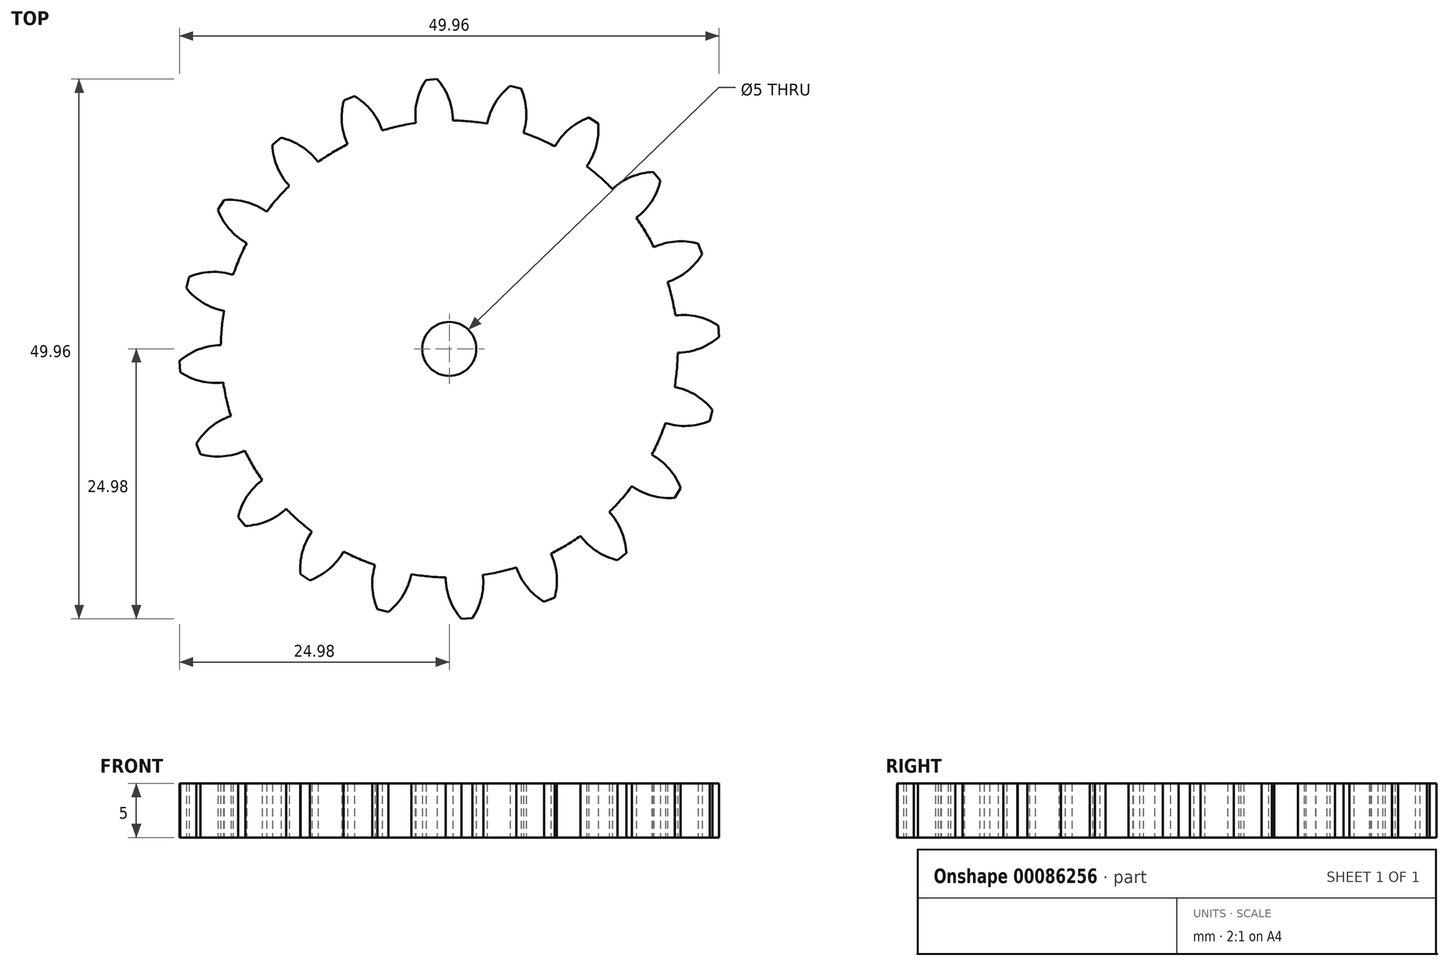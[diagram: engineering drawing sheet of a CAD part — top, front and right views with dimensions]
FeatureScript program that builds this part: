
annotation { "Feature Type Name" : "Feature", "Feature Type Description" : "" }
export const myFeature = defineFeature(function(context is Context, id is Id, definition is map)
    precondition{}
    {
        {
            assignVariable(context, id + "F0", {"name" : "GearDepth", "anyValue" : 5});
        }
        {
            var Q0;
            Q0=qCreatedBy(makeId("Top.planeOp"),FACE);
            var sketch = newSketch(context, id + "F1", { "sketchPlane" : qUnion([Q0])});
            skCircle(sketch, "E0", {"center": v(0, 0) * mm, "radius": 21.15 * mm});
            skCircle(sketch, "E1", {"center": v(0, 0) * mm, "radius": 23.08 * mm, "construction": true});
            skCircle(sketch, "E2", {"center": v(0, 0) * mm, "radius": 25 * mm, "construction": true});
            skLineSegment(sketch, "E3", {"start": v(0, 0) * mm, "end": v(0, 17.6) * mm, "construction": true});
            skLineSegment(sketch, "E4", {"start": v(0, 0) * mm, "end": v(-1.18, 18.01) * mm, "construction": true});
            skLineSegment(sketch, "E5", {"start": v(0, 23.08) * mm, "end": v(-10.54, 23.08) * mm, "construction": true});
            skLineSegment(sketch, "E6", {"start": v(0, 23.08) * mm, "end": v(-10.3, 19.33) * mm, "construction": true});
            skCircle(sketch, "E7", {"center": v(0, 23.08) * mm, "radius": 5.77 * mm, "construction": true});
            skCircle(sketch, "E8", {"center": v(-5.42, 21.1) * mm, "radius": 5.77 * mm, "construction": true});
            skArc(sketch, "E9", {"start": v(-10.84, 23.08) * mm, "mid": v(-10.95, 22.76) * mm, "end": v(-11.04, 22.43) * mm});
            skArc(sketch, "E10.trimOffspring", {"start": v(0.34, 21.15) * mm, "mid": v(-0.04, 23.2) * mm, "end": v(-1.11, 24.98) * mm});
            skArc(sketch, "E11.MirrorCS", {"start": v(-3.1, 20.93) * mm, "mid": v(-2.98, 23) * mm, "end": v(-2.16, 24.9) * mm});
            skLineSegment(sketch, "E12", {"start": v(-2.16, 24.9) * mm, "end": v(-1.11, 24.98) * mm});
            skArc(sketch, "E13.1.0", {"start": v(-6.2, 20.22) * mm, "mid": v(-7.2, 22.05) * mm, "end": v(-8.78, 23.4) * mm});
            skLineSegment(sketch, "E13.1.1", {"start": v(-9.75, 23.02) * mm, "end": v(-8.78, 23.4) * mm});
            skArc(sketch, "E13.1.2", {"start": v(-9.42, 18.94) * mm, "mid": v(-9.95, 20.95) * mm, "end": v(-9.75, 23.02) * mm});
            skArc(sketch, "E13.2.0", {"start": v(-12.15, 17.31) * mm, "mid": v(-13.67, 18.74) * mm, "end": v(-15.58, 19.55) * mm});
            skLineSegment(sketch, "E13.2.1", {"start": v(-16.38, 18.88) * mm, "end": v(-15.58, 19.55) * mm});
            skArc(sketch, "E13.2.2", {"start": v(-14.8, 15.1) * mm, "mid": v(-15.93, 16.85) * mm, "end": v(-16.38, 18.88) * mm});
            skArc(sketch, "E13.3.0", {"start": v(-16.9, 12.71) * mm, "mid": v(-18.79, 13.6) * mm, "end": v(-20.86, 13.78) * mm});
            skLineSegment(sketch, "E13.3.1", {"start": v(-21.42, 12.9) * mm, "end": v(-20.86, 13.78) * mm});
            skArc(sketch, "E13.3.2", {"start": v(-18.75, 9.79) * mm, "mid": v(-20.36, 11.1) * mm, "end": v(-21.42, 12.9) * mm});
            skArc(sketch, "E13.4.0", {"start": v(-20, 6.86) * mm, "mid": v(-22.07, 7.13) * mm, "end": v(-24.1, 6.66) * mm});
            skLineSegment(sketch, "E13.4.1", {"start": v(-24.35, 5.65) * mm, "end": v(-24.1, 6.66) * mm});
            skArc(sketch, "E13.4.2", {"start": v(-20.86, 3.52) * mm, "mid": v(-22.8, 4.27) * mm, "end": v(-24.35, 5.65) * mm});
            skArc(sketch, "E13.5.0", {"start": v(-21.15, 0.34) * mm, "mid": v(-23.2, -0.04) * mm, "end": v(-24.98, -1.11) * mm});
            skLineSegment(sketch, "E13.5.1", {"start": v(-24.9, -2.16) * mm, "end": v(-24.98, -1.11) * mm});
            skArc(sketch, "E13.5.2", {"start": v(-20.93, -3.1) * mm, "mid": v(-23, -2.98) * mm, "end": v(-24.9, -2.16) * mm});
            skArc(sketch, "E13.6.0", {"start": v(-20.22, -6.2) * mm, "mid": v(-22.05, -7.2) * mm, "end": v(-23.4, -8.78) * mm});
            skLineSegment(sketch, "E13.6.1", {"start": v(-23.02, -9.75) * mm, "end": v(-23.4, -8.78) * mm});
            skArc(sketch, "E13.6.2", {"start": v(-18.94, -9.42) * mm, "mid": v(-20.95, -9.95) * mm, "end": v(-23.02, -9.75) * mm});
            skArc(sketch, "E13.7.0", {"start": v(-17.31, -12.15) * mm, "mid": v(-18.74, -13.67) * mm, "end": v(-19.55, -15.58) * mm});
            skLineSegment(sketch, "E13.7.1", {"start": v(-18.88, -16.38) * mm, "end": v(-19.55, -15.58) * mm});
            skArc(sketch, "E13.7.2", {"start": v(-15.1, -14.8) * mm, "mid": v(-16.85, -15.93) * mm, "end": v(-18.88, -16.38) * mm});
            skArc(sketch, "E13.8.0", {"start": v(-12.71, -16.9) * mm, "mid": v(-13.6, -18.79) * mm, "end": v(-13.78, -20.86) * mm});
            skLineSegment(sketch, "E13.8.1", {"start": v(-12.9, -21.42) * mm, "end": v(-13.78, -20.86) * mm});
            skArc(sketch, "E13.8.2", {"start": v(-9.79, -18.75) * mm, "mid": v(-11.1, -20.36) * mm, "end": v(-12.9, -21.42) * mm});
            skArc(sketch, "E13.9.0", {"start": v(-6.86, -20) * mm, "mid": v(-7.13, -22.07) * mm, "end": v(-6.66, -24.1) * mm});
            skLineSegment(sketch, "E13.9.1", {"start": v(-5.65, -24.35) * mm, "end": v(-6.66, -24.1) * mm});
            skArc(sketch, "E13.9.2", {"start": v(-3.52, -20.86) * mm, "mid": v(-4.27, -22.8) * mm, "end": v(-5.65, -24.35) * mm});
            skArc(sketch, "E13.10.0", {"start": v(-0.34, -21.15) * mm, "mid": v(0.04, -23.2) * mm, "end": v(1.11, -24.98) * mm});
            skLineSegment(sketch, "E13.10.1", {"start": v(2.16, -24.9) * mm, "end": v(1.11, -24.98) * mm});
            skArc(sketch, "E13.10.2", {"start": v(3.1, -20.93) * mm, "mid": v(2.98, -23) * mm, "end": v(2.16, -24.9) * mm});
            skArc(sketch, "E13.11.0", {"start": v(6.2, -20.22) * mm, "mid": v(7.2, -22.05) * mm, "end": v(8.78, -23.4) * mm});
            skLineSegment(sketch, "E13.11.1", {"start": v(9.75, -23.02) * mm, "end": v(8.78, -23.4) * mm});
            skArc(sketch, "E13.11.2", {"start": v(9.42, -18.94) * mm, "mid": v(9.95, -20.95) * mm, "end": v(9.75, -23.02) * mm});
            skArc(sketch, "E13.12.0", {"start": v(12.15, -17.31) * mm, "mid": v(13.67, -18.74) * mm, "end": v(15.58, -19.55) * mm});
            skLineSegment(sketch, "E13.12.1", {"start": v(16.38, -18.88) * mm, "end": v(15.58, -19.55) * mm});
            skArc(sketch, "E13.12.2", {"start": v(14.8, -15.1) * mm, "mid": v(15.93, -16.85) * mm, "end": v(16.38, -18.88) * mm});
            skArc(sketch, "E13.13.0", {"start": v(16.9, -12.71) * mm, "mid": v(18.79, -13.6) * mm, "end": v(20.86, -13.78) * mm});
            skLineSegment(sketch, "E13.13.1", {"start": v(21.42, -12.9) * mm, "end": v(20.86, -13.78) * mm});
            skArc(sketch, "E13.13.2", {"start": v(18.75, -9.79) * mm, "mid": v(20.36, -11.1) * mm, "end": v(21.42, -12.9) * mm});
            skArc(sketch, "E13.14.0", {"start": v(20, -6.86) * mm, "mid": v(22.07, -7.13) * mm, "end": v(24.1, -6.66) * mm});
            skLineSegment(sketch, "E13.14.1", {"start": v(24.35, -5.65) * mm, "end": v(24.1, -6.66) * mm});
            skArc(sketch, "E13.14.2", {"start": v(20.86, -3.52) * mm, "mid": v(22.8, -4.27) * mm, "end": v(24.35, -5.65) * mm});
            skArc(sketch, "E13.15.0", {"start": v(21.15, -0.34) * mm, "mid": v(23.2, 0.04) * mm, "end": v(24.98, 1.11) * mm});
            skLineSegment(sketch, "E13.15.1", {"start": v(24.9, 2.16) * mm, "end": v(24.98, 1.11) * mm});
            skArc(sketch, "E13.15.2", {"start": v(20.93, 3.1) * mm, "mid": v(23, 2.98) * mm, "end": v(24.9, 2.16) * mm});
            skArc(sketch, "E13.16.0", {"start": v(20.22, 6.2) * mm, "mid": v(22.05, 7.2) * mm, "end": v(23.4, 8.78) * mm});
            skLineSegment(sketch, "E13.16.1", {"start": v(23.02, 9.75) * mm, "end": v(23.4, 8.78) * mm});
            skArc(sketch, "E13.16.2", {"start": v(18.94, 9.42) * mm, "mid": v(20.95, 9.95) * mm, "end": v(23.02, 9.75) * mm});
            skArc(sketch, "E13.17.0", {"start": v(17.31, 12.15) * mm, "mid": v(18.74, 13.67) * mm, "end": v(19.55, 15.58) * mm});
            skLineSegment(sketch, "E13.17.1", {"start": v(18.88, 16.38) * mm, "end": v(19.55, 15.58) * mm});
            skArc(sketch, "E13.17.2", {"start": v(15.1, 14.8) * mm, "mid": v(16.85, 15.93) * mm, "end": v(18.88, 16.38) * mm});
            skArc(sketch, "E13.18.0", {"start": v(12.71, 16.9) * mm, "mid": v(13.6, 18.79) * mm, "end": v(13.78, 20.86) * mm});
            skLineSegment(sketch, "E13.18.1", {"start": v(12.9, 21.42) * mm, "end": v(13.78, 20.86) * mm});
            skArc(sketch, "E13.18.2", {"start": v(9.79, 18.75) * mm, "mid": v(11.1, 20.36) * mm, "end": v(12.9, 21.42) * mm});
            skArc(sketch, "E13.19.0", {"start": v(6.86, 20) * mm, "mid": v(7.13, 22.07) * mm, "end": v(6.66, 24.1) * mm});
            skLineSegment(sketch, "E13.19.1", {"start": v(5.65, 24.35) * mm, "end": v(6.66, 24.1) * mm});
            skArc(sketch, "E13.19.2", {"start": v(3.52, 20.86) * mm, "mid": v(4.27, 22.8) * mm, "end": v(5.65, 24.35) * mm});
            skCircle(sketch, "E14", {"center": v(0, 0) * mm, "radius": 2.5 * mm});
            skSolve(sketch);
        }
        {
            var Q0;
            {var subQ0=sQuery(id+"F1.wireOp",EDGE,"E10.trimOffspring");Q0=makeQuery(id+"F1.imprint","IMPRINT",FACE,{"disambiguationData":[TD([[makeQuery(id+"F1.imprint","IMPRINT",EDGE,{"derivedFrom":subQ0}),1.0]])]});}
            var Q1;
            {var subQ0=sQuery(id+"F1.wireOp",EDGE,"E0");var subQ1=makeQuery(id+"F1.imprint","INTERSECT",VERTEX,{"derivedFrom":[subQ0,sQuery(id+"F1.wireOp",EDGE,"E10.trimOffspring")]});Q1=makeQuery(id+"F1.imprint","IMPRINT",FACE,{"disambiguationData":[TD([[makeQuery(id+"F1.imprint","IMPRINT",EDGE,{"disambiguationData":[TD([[subQ1,-1.0]])],"derivedFrom":subQ0}),1.0]])]});}
            var Q2;
            {var subQ0=sQuery(id+"F1.wireOp",EDGE,"E13.1.0");Q2=makeQuery(id+"F1.imprint","IMPRINT",FACE,{"disambiguationData":[TD([[makeQuery(id+"F1.imprint","IMPRINT",EDGE,{"derivedFrom":subQ0}),1.0]])]});}
            var Q3;
            {var subQ0=sQuery(id+"F1.wireOp",EDGE,"E13.2.0");Q3=makeQuery(id+"F1.imprint","IMPRINT",FACE,{"disambiguationData":[TD([[makeQuery(id+"F1.imprint","IMPRINT",EDGE,{"derivedFrom":subQ0}),1.0]])]});}
            var Q4;
            {var subQ0=sQuery(id+"F1.wireOp",EDGE,"E13.3.0");Q4=makeQuery(id+"F1.imprint","IMPRINT",FACE,{"disambiguationData":[TD([[makeQuery(id+"F1.imprint","IMPRINT",EDGE,{"derivedFrom":subQ0}),1.0]])]});}
            var Q5;
            {var subQ0=sQuery(id+"F1.wireOp",EDGE,"E13.4.0");Q5=makeQuery(id+"F1.imprint","IMPRINT",FACE,{"disambiguationData":[TD([[makeQuery(id+"F1.imprint","IMPRINT",EDGE,{"derivedFrom":subQ0}),1.0]])]});}
            var Q6;
            {var subQ0=sQuery(id+"F1.wireOp",EDGE,"E13.5.0");Q6=makeQuery(id+"F1.imprint","IMPRINT",FACE,{"disambiguationData":[TD([[makeQuery(id+"F1.imprint","IMPRINT",EDGE,{"derivedFrom":subQ0}),1.0]])]});}
            var Q7;
            {var subQ0=sQuery(id+"F1.wireOp",EDGE,"E13.6.0");Q7=makeQuery(id+"F1.imprint","IMPRINT",FACE,{"disambiguationData":[TD([[makeQuery(id+"F1.imprint","IMPRINT",EDGE,{"derivedFrom":subQ0}),1.0]])]});}
            var Q8;
            {var subQ0=sQuery(id+"F1.wireOp",EDGE,"E13.7.0");Q8=makeQuery(id+"F1.imprint","IMPRINT",FACE,{"disambiguationData":[TD([[makeQuery(id+"F1.imprint","IMPRINT",EDGE,{"derivedFrom":subQ0}),1.0]])]});}
            var Q9;
            {var subQ0=sQuery(id+"F1.wireOp",EDGE,"E13.8.0");Q9=makeQuery(id+"F1.imprint","IMPRINT",FACE,{"disambiguationData":[TD([[makeQuery(id+"F1.imprint","IMPRINT",EDGE,{"derivedFrom":subQ0}),1.0]])]});}
            var Q10;
            {var subQ0=sQuery(id+"F1.wireOp",EDGE,"E13.9.0");Q10=makeQuery(id+"F1.imprint","IMPRINT",FACE,{"disambiguationData":[TD([[makeQuery(id+"F1.imprint","IMPRINT",EDGE,{"derivedFrom":subQ0}),1.0]])]});}
            var Q11;
            {var subQ0=sQuery(id+"F1.wireOp",EDGE,"E13.10.0");Q11=makeQuery(id+"F1.imprint","IMPRINT",FACE,{"disambiguationData":[TD([[makeQuery(id+"F1.imprint","IMPRINT",EDGE,{"derivedFrom":subQ0}),1.0]])]});}
            var Q12;
            {var subQ0=sQuery(id+"F1.wireOp",EDGE,"E13.11.0");Q12=makeQuery(id+"F1.imprint","IMPRINT",FACE,{"disambiguationData":[TD([[makeQuery(id+"F1.imprint","IMPRINT",EDGE,{"derivedFrom":subQ0}),1.0]])]});}
            var Q13;
            {var subQ0=sQuery(id+"F1.wireOp",EDGE,"E13.12.0");Q13=makeQuery(id+"F1.imprint","IMPRINT",FACE,{"disambiguationData":[TD([[makeQuery(id+"F1.imprint","IMPRINT",EDGE,{"derivedFrom":subQ0}),1.0]])]});}
            var Q14;
            {var subQ0=sQuery(id+"F1.wireOp",EDGE,"E13.13.0");Q14=makeQuery(id+"F1.imprint","IMPRINT",FACE,{"disambiguationData":[TD([[makeQuery(id+"F1.imprint","IMPRINT",EDGE,{"derivedFrom":subQ0}),1.0]])]});}
            var Q15;
            {var subQ0=sQuery(id+"F1.wireOp",EDGE,"E13.14.0");Q15=makeQuery(id+"F1.imprint","IMPRINT",FACE,{"disambiguationData":[TD([[makeQuery(id+"F1.imprint","IMPRINT",EDGE,{"derivedFrom":subQ0}),1.0]])]});}
            var Q16;
            {var subQ0=sQuery(id+"F1.wireOp",EDGE,"E13.15.0");Q16=makeQuery(id+"F1.imprint","IMPRINT",FACE,{"disambiguationData":[TD([[makeQuery(id+"F1.imprint","IMPRINT",EDGE,{"derivedFrom":subQ0}),1.0]])]});}
            var Q17;
            {var subQ0=sQuery(id+"F1.wireOp",EDGE,"E13.16.0");Q17=makeQuery(id+"F1.imprint","IMPRINT",FACE,{"disambiguationData":[TD([[makeQuery(id+"F1.imprint","IMPRINT",EDGE,{"derivedFrom":subQ0}),1.0]])]});}
            var Q18;
            {var subQ0=sQuery(id+"F1.wireOp",EDGE,"E13.17.0");Q18=makeQuery(id+"F1.imprint","IMPRINT",FACE,{"disambiguationData":[TD([[makeQuery(id+"F1.imprint","IMPRINT",EDGE,{"derivedFrom":subQ0}),1.0]])]});}
            var Q19;
            {var subQ0=sQuery(id+"F1.wireOp",EDGE,"E13.18.0");Q19=makeQuery(id+"F1.imprint","IMPRINT",FACE,{"disambiguationData":[TD([[makeQuery(id+"F1.imprint","IMPRINT",EDGE,{"derivedFrom":subQ0}),1.0]])]});}
            var Q20;
            {var subQ0=sQuery(id+"F1.wireOp",EDGE,"E13.19.0");Q20=makeQuery(id+"F1.imprint","IMPRINT",FACE,{"disambiguationData":[TD([[makeQuery(id+"F1.imprint","IMPRINT",EDGE,{"derivedFrom":subQ0}),1.0]])]});}
            var Q21;
            Q21=sQuery(id+"F1.wireOp",EDGE,"E0");
            var Q22;
            Q22=sQuery(id+"F1.wireOp",EDGE,"E10.trimOffspring");
            var Q23;
            Q23=sQuery(id+"F1.wireOp",EDGE,"E12");
            var Q24;
            Q24=sQuery(id+"F1.wireOp",EDGE,"E11.MirrorCS");
            extrude(context, id + "F2", {"entities" : qUnion([Q0, Q1, Q2, Q3, Q4, Q5, Q6, Q7, Q8, Q9, Q10, Q11, Q12, Q13, Q14, Q15, Q16, Q17, Q18, Q19, Q20]), "surfaceEntities" : qUnion([Q21, Q22, Q23, Q24]), "depth" : (getVariable(context, 'GearDepth')) * mm});
        }
    });
